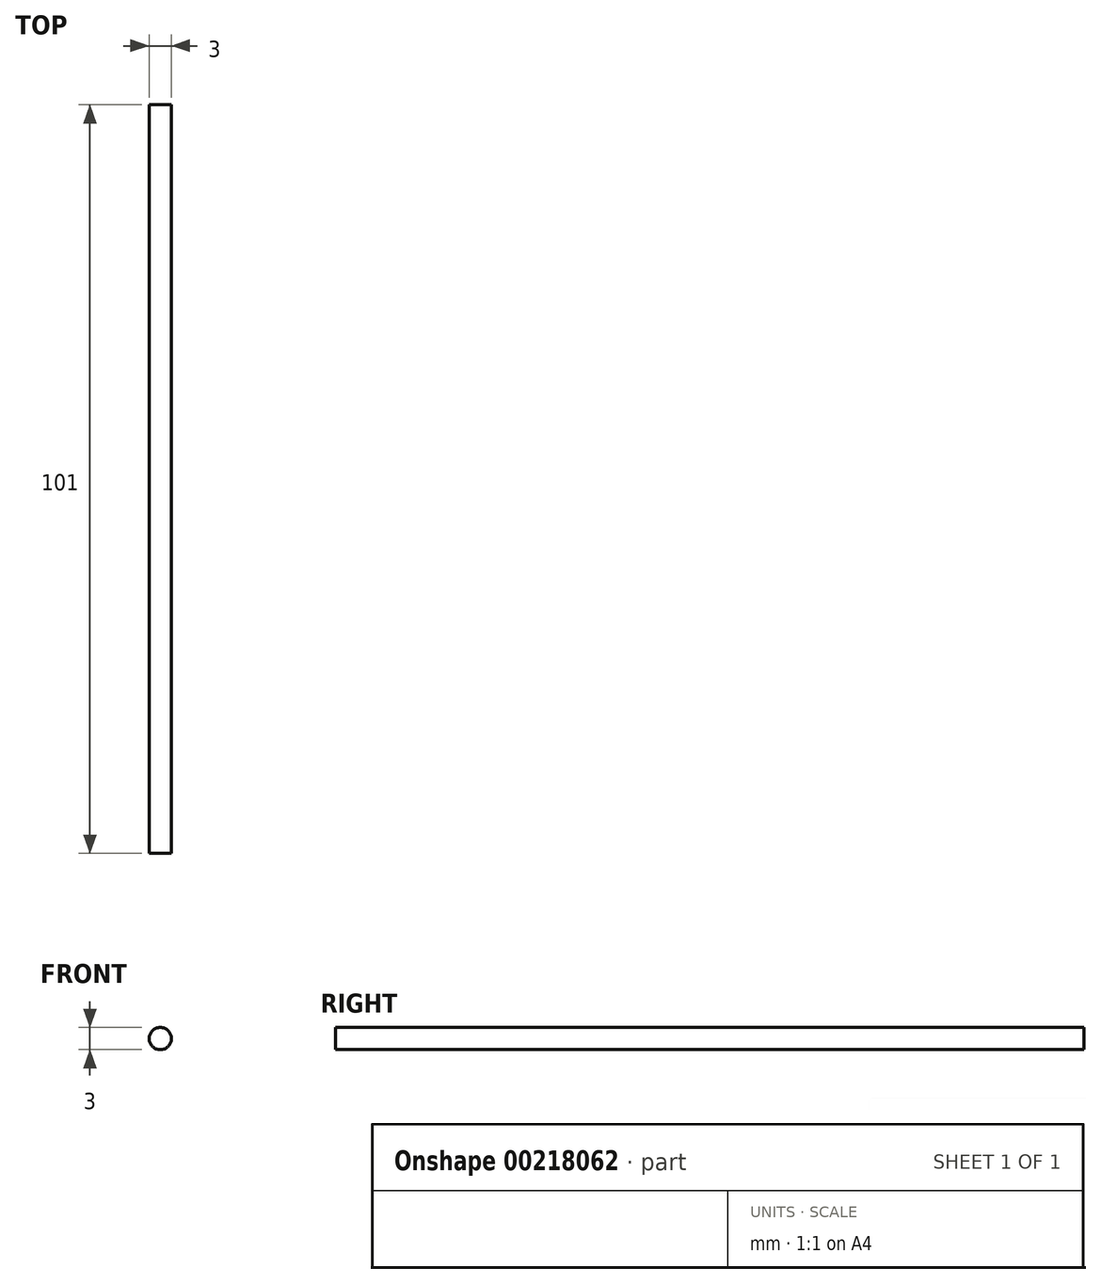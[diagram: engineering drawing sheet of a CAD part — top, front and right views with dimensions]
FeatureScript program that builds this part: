
annotation { "Feature Type Name" : "Feature", "Feature Type Description" : "" }
export const myFeature = defineFeature(function(context is Context, id is Id, definition is map)
    precondition{}
    {
        {
            var Q0;
            Q0=qCreatedBy(makeId("Front.planeOp"),FACE);
            var sketch = newSketch(context, id + "F0", { "sketchPlane" : qUnion([Q0])});
            skCircle(sketch, "E0", {"center": v(18.68, 12.5) * mm, "radius": 1.5 * mm});
            skSolve(sketch);
        }
        {
            var Q0;
            Q0=makeQuery(id+"F0.imprint","IMPRINT",FACE,{"disambiguationData":[TD([[makeQuery(id+"F0.imprint","IMPRINT",EDGE,{"derivedFrom":sQuery(id+"F0.wireOp",EDGE,"E0")}),1.0]])]});
            extrude(context, id + "F1", {"entities" : qUnion([Q0]), "depth" : 101 * mm});
        }
    });
